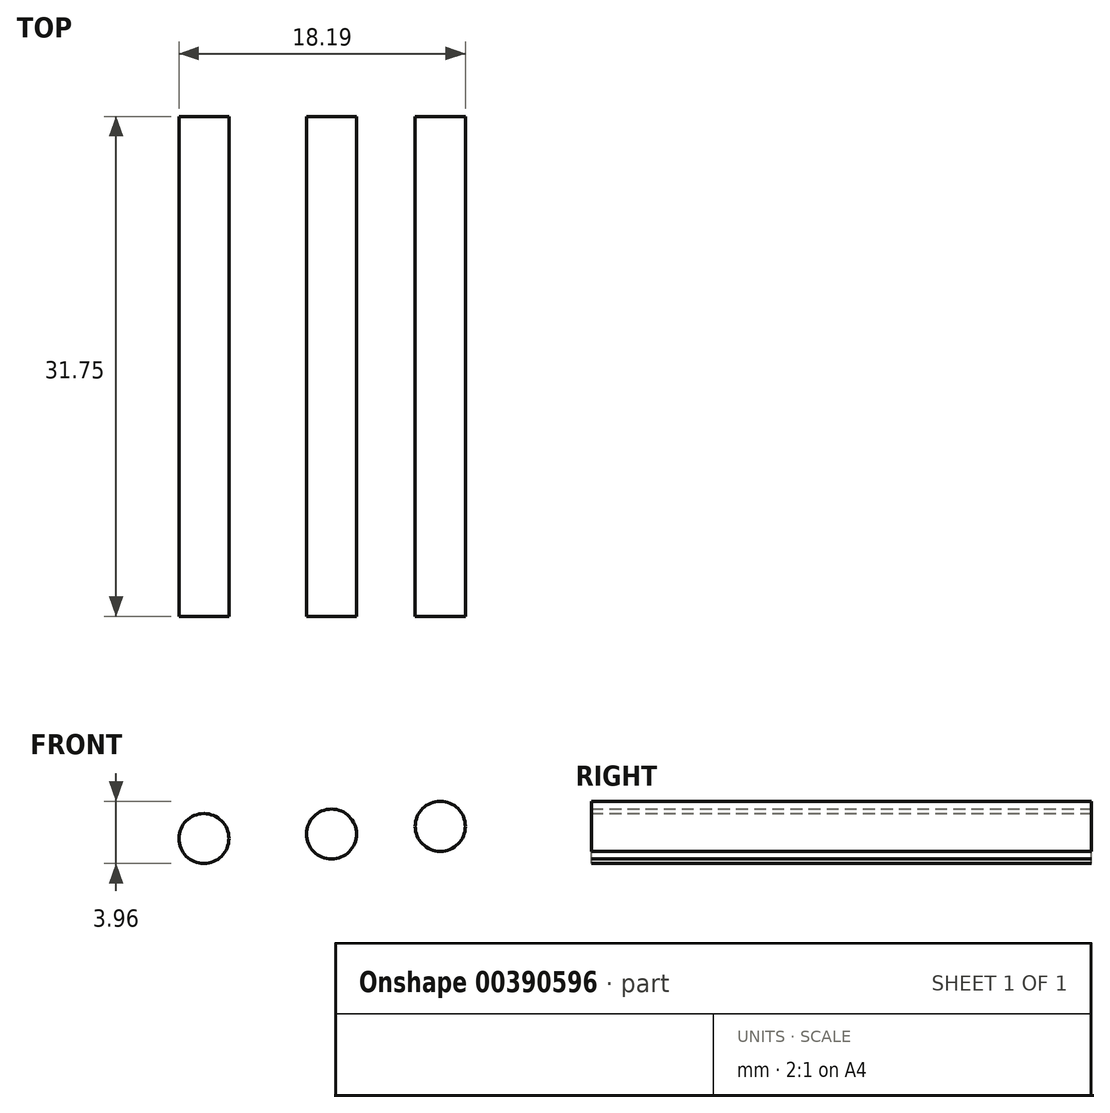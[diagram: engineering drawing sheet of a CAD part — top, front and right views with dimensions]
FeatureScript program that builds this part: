
annotation { "Feature Type Name" : "Feature", "Feature Type Description" : "" }
export const myFeature = defineFeature(function(context is Context, id is Id, definition is map)
    precondition{}
    {
        {
            var Q0;
            Q0=qCreatedBy(makeId("Front.planeOp"),FACE);
            var sketch = newSketch(context, id + "F0", { "sketchPlane" : qUnion([Q0])});
            skCircle(sketch, "E0", {"center": v(-33.84, 11.94) * mm, "radius": 1.59 * mm});
            skCircle(sketch, "E1", {"center": v(-25.73, 12.22) * mm, "radius": 1.59 * mm});
            skCircle(sketch, "E2", {"center": v(-18.83, 12.71) * mm, "radius": 1.6 * mm});
            skSolve(sketch);
        }
        {
            var Q0;
            Q0 = qSketchRegion(id + "F0", true);
            extrude(context, id + "F1", {"entities" : qUnion([Q0]), "depth" : 31.75 * mm});
        }
    });
